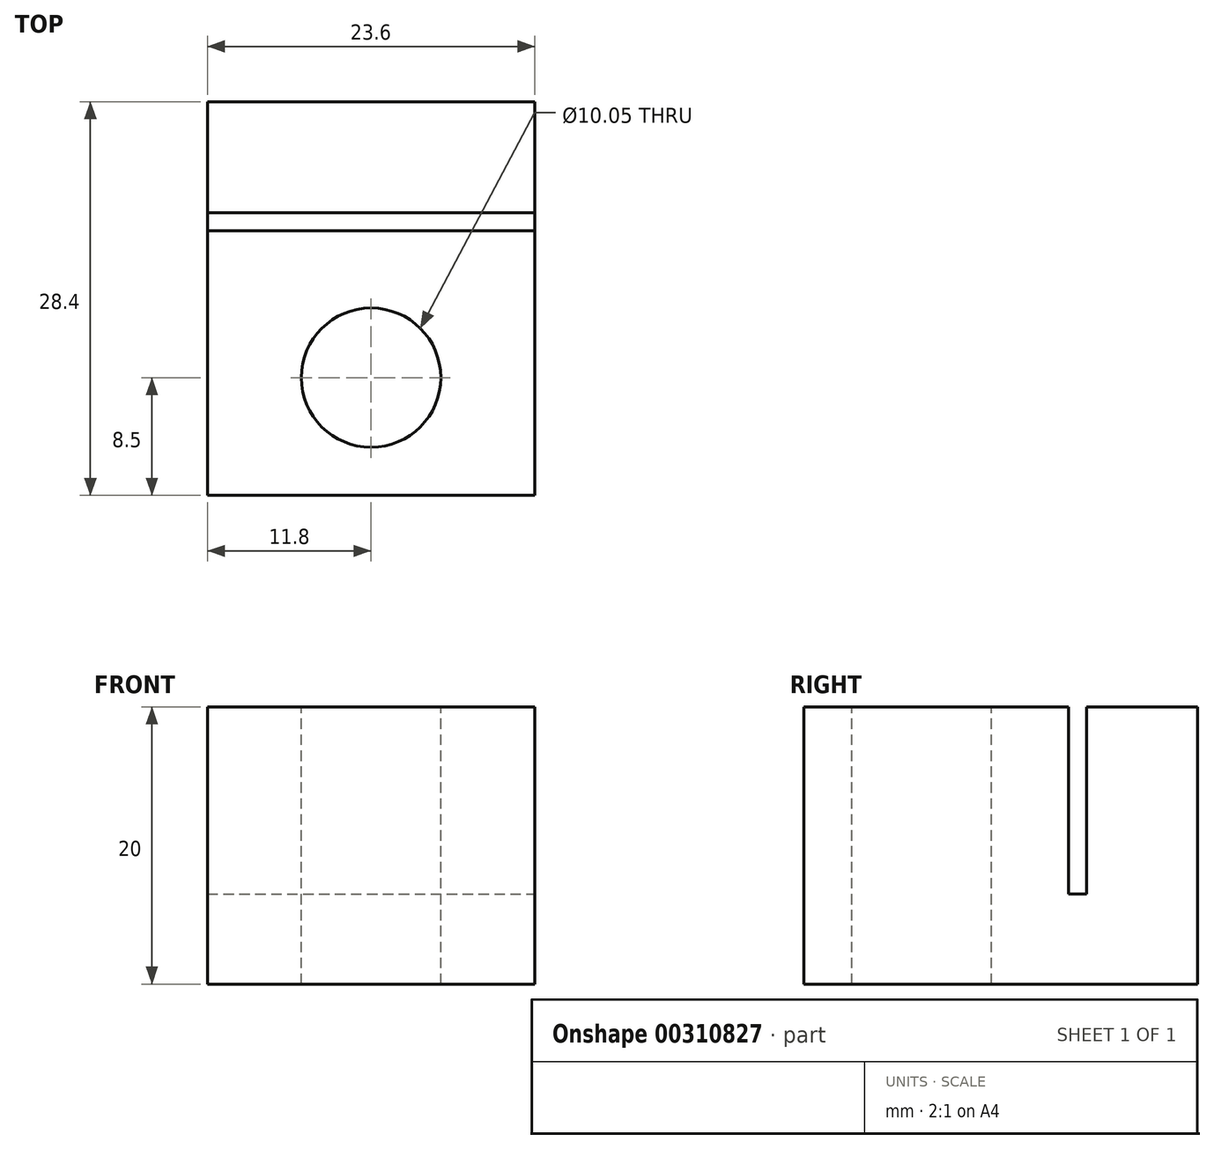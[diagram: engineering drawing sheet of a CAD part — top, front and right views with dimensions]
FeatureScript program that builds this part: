
annotation { "Feature Type Name" : "Feature", "Feature Type Description" : "" }
export const myFeature = defineFeature(function(context is Context, id is Id, definition is map)
    precondition{}
    {
        {
            var Q0;
            Q0=qCreatedBy(makeId("Top.planeOp"),FACE);
            var sketch = newSketch(context, id + "F0", { "sketchPlane" : qUnion([Q0])});
            skLineSegment(sketch, "E0.bottom", {"start": v(11.8, 14.2) * mm, "end": v(-11.8, 14.2) * mm});
            skLineSegment(sketch, "E0.top", {"start": v(11.8, -14.2) * mm, "end": v(-11.8, -14.2) * mm});
            skLineSegment(sketch, "E0.left", {"start": v(11.8, 14.2) * mm, "end": v(11.8, -14.2) * mm});
            skLineSegment(sketch, "E0.right", {"start": v(-11.8, 14.2) * mm, "end": v(-11.8, -14.2) * mm});
            skPoint(sketch, "E0.middle", {"position": v(0, 0) * mm});
            skSolve(sketch);
        }
        {
            var Q0;
            Q0 = qSketchRegion(id + "F0", true);
            extrude(context, id + "F1", {"entities" : qUnion([Q0]), "depth" : 20 * mm});
        }
        {
            var Q0;
            Q0=makeQuery(id+"F1.opExtrude","CAP_FACE",FACE,{"disambiguationData":[OSD([sQuery(id+"F0.wireOp",EDGE,"E0.bottom"),sQuery(id+"F0.wireOp",EDGE,"E0.top"),sQuery(id+"F0.wireOp",EDGE,"E0.left"),sQuery(id+"F0.wireOp",EDGE,"E0.right")])],"isStart":false});
            var sketch = newSketch(context, id + "F2", { "sketchPlane" : qUnion([Q0])});
            skLineSegment(sketch, "E1.bottom", {"start": v(-11.8, 6.2) * mm, "end": v(11.8, 6.2) * mm});
            skLineSegment(sketch, "E1.top", {"start": v(-11.8, 4.9) * mm, "end": v(11.8, 4.9) * mm});
            skLineSegment(sketch, "E1.left", {"start": v(-11.8, 6.2) * mm, "end": v(-11.8, 4.9) * mm});
            skLineSegment(sketch, "E1.right", {"start": v(11.8, 6.2) * mm, "end": v(11.8, 4.9) * mm});
            skCircle(sketch, "E2", {"center": v(0, -5.7) * mm, "radius": 5.03 * mm});
            skSolve(sketch);
        }
        {
            var Q0;
            Q0=makeQuery(id+"F2.imprint","IMPRINT",FACE,{"disambiguationData":[TD([[makeQuery(id+"F2.imprint","IMPRINT",EDGE,{"derivedFrom":sQuery(id+"F2.wireOp",EDGE,"E1.bottom")}),-1.0]])]});
            extrude(context, id + "F3", {"entities" : qUnion([Q0]), "operationType" : NewBodyOperationType.REMOVE, "oppositeDirection" : true, "depth" : 13.5 * mm});
        }
        {
            var Q0;
            Q0=makeQuery(id+"F2.imprint","IMPRINT",FACE,{"disambiguationData":[TD([[makeQuery(id+"F2.imprint","IMPRINT",EDGE,{"derivedFrom":sQuery(id+"F2.wireOp",EDGE,"E2")}),1.0]])]});
            extrude(context, id + "F4", {"entities" : qUnion([Q0]), "operationType" : NewBodyOperationType.REMOVE, "endBound" : BoundingType.THROUGH_ALL, "oppositeDirection" : true, "depth" : 25 * mm});
        }
    });
